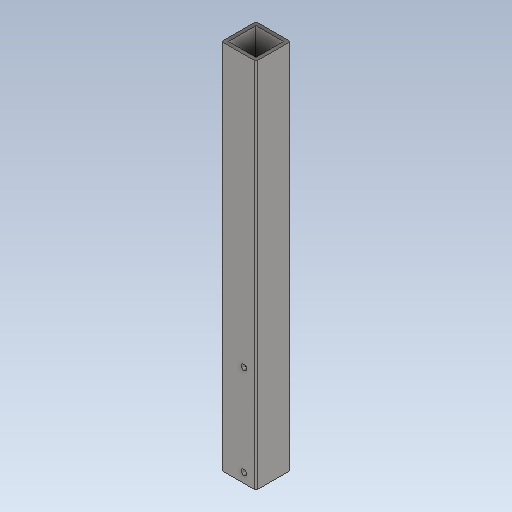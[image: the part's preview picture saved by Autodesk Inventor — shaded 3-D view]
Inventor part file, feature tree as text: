
AUTODESK INVENTOR PART (.ipt)
format: ipt  version: 2021 (Build 250183000, 183)  size: 159,232 bytes
history: native  units: mm
features: sketch x2, extrude x1, fillet x1, hole x1
ambient origin geometry x8: Origin, YZ Plane, XZ Plane, XY Plane, X Axis, Y Axis, Z Axis, Center Point
bodies: Solid1 (feature_tree)
feature tree (5):
  extrude  "Extrusion1"  Depth=50.0mm
  fillet  "Fillet1"  Radius=25.0mm
  hole  "Hole1"  [1 undecoded]
  sketch  "Sketch1"  dims[d0=50.0mm d1=50.0mm d2=25.0mm]
  sketch  "Sketch2"  dims[d3=25.0mm d4=5.0mm d5=539.0mm d6=0.0mm d7=2.0mm d12=8.0mm d13=6.0mm d14=4.0mm d15=2.0mm d16=90.0deg d17=8.0mm d18=20.594885mm d19=459.214mm d22=66.0mm d23=66.0mm d24=17.5mm d25=0.0mm]
note: 1 required parameter value undecoded (feature->parameter linkage not recoverable at this tier; creation-order binding heuristic only, values carry confidence <= 0.55)
